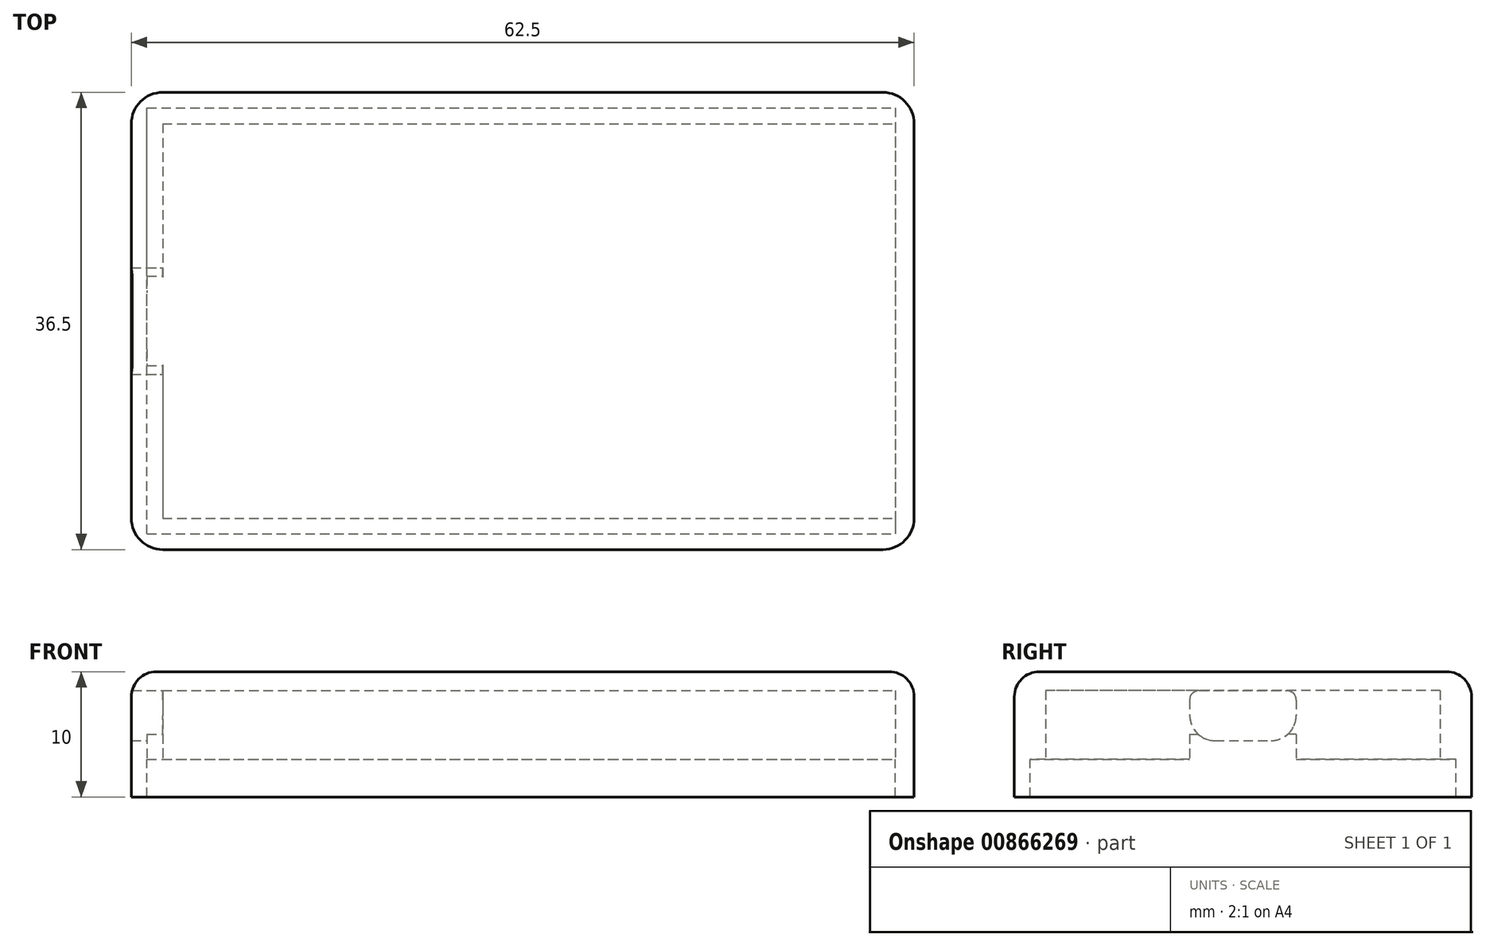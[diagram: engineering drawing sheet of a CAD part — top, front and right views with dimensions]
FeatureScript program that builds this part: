
annotation { "Feature Type Name" : "Feature", "Feature Type Description" : "" }
export const myFeature = defineFeature(function(context is Context, id is Id, definition is map)
    precondition{}
    {
        {
            var Q0;
            Q0=qCreatedBy(makeId("Top.planeOp"),FACE);
            var sketch = newSketch(context, id + "F0", { "sketchPlane" : qUnion([Q0])});
            skLineSegment(sketch, "E0.bottom", {"start": v(-30.75, 18.75) * mm, "end": v(31.75, 18.75) * mm});
            skLineSegment(sketch, "E0.top", {"start": v(-30.75, -17.75) * mm, "end": v(31.75, -17.75) * mm});
            skLineSegment(sketch, "E0.left", {"start": v(-30.75, 18.75) * mm, "end": v(-30.75, -17.75) * mm});
            skLineSegment(sketch, "E0.right", {"start": v(31.75, 18.75) * mm, "end": v(31.75, -17.75) * mm});
            skLineSegment(sketch, "E1.bottom", {"start": v(-28.25, 16.25) * mm, "end": v(30.25, 16.25) * mm});
            skLineSegment(sketch, "E1.top", {"start": v(-28.25, -15.25) * mm, "end": v(30.25, -15.25) * mm});
            skLineSegment(sketch, "E1.left", {"start": v(-28.25, 16.25) * mm, "end": v(-28.25, -15.25) * mm});
            skLineSegment(sketch, "E1.right", {"start": v(30.25, 16.25) * mm, "end": v(30.25, -15.25) * mm});
            skSolve(sketch);
        }
        {
            var Q0;
            Q0=makeQuery(id+"F0.imprint","IMPRINT",FACE,{"disambiguationData":[TD([[makeQuery(id+"F0.imprint","IMPRINT",EDGE,{"derivedFrom":sQuery(id+"F0.wireOp",EDGE,"E0.bottom")}),-1.0]])]});
            extrude(context, id + "F1", {"entities" : qUnion([Q0]), "depth" : 7 * mm});
        }
        {
            var Q0;
            Q0=makeQuery(id+"F1.opExtrude","CAP_FACE",FACE,{"disambiguationData":[OSD([sQuery(id+"F0.wireOp",EDGE,"E0.bottom"),sQuery(id+"F0.wireOp",EDGE,"E0.top"),sQuery(id+"F0.wireOp",EDGE,"E0.left"),sQuery(id+"F0.wireOp",EDGE,"E0.right"),sQuery(id+"F0.wireOp",EDGE,"E1.bottom"),sQuery(id+"F0.wireOp",EDGE,"E1.top"),sQuery(id+"F0.wireOp",EDGE,"E1.left"),sQuery(id+"F0.wireOp",EDGE,"E1.right")])],"isStart":false});
            var sketch = newSketch(context, id + "F2", { "sketchPlane" : qUnion([Q0])});
            skLineSegment(sketch, "E2.bottom", {"start": v(-28.25, 16.25) * mm, "end": v(30.25, 16.25) * mm});
            skLineSegment(sketch, "E2.top", {"start": v(-28.25, -15.25) * mm, "end": v(30.25, -15.25) * mm});
            skLineSegment(sketch, "E2.left", {"start": v(-28.25, 16.25) * mm, "end": v(-28.25, -15.25) * mm});
            skLineSegment(sketch, "E3", {"start": v(30.25, 16.25) * mm, "end": v(30.25, 7) * mm});
            skLineSegment(sketch, "E4", {"start": v(30.25, -6) * mm, "end": v(30.25, -15.25) * mm});
            skSolve(sketch);
        }
        {
            var Q0;
            Q0=makeQuery(id+"F2.imprint","IMPRINT",FACE,{"disambiguationData":[TD([[makeQuery(id+"F2.imprint","IMPRINT",EDGE,{"derivedFrom":sQuery(id+"F2.wireOp",EDGE,"E2.bottom")}),-1.0]])]});
            extrude(context, id + "F3", {"entities" : qUnion([Q0]), "operationType" : NewBodyOperationType.ADD, "oppositeDirection" : true, "depth" : 1.5 * mm});
        }
        {
            var Q0;
            Q0=makeQuery(id+"F1.opExtrude","CAP_FACE",FACE,{"disambiguationData":[OSD([sQuery(id+"F0.wireOp",EDGE,"E0.bottom"),sQuery(id+"F0.wireOp",EDGE,"E0.top"),sQuery(id+"F0.wireOp",EDGE,"E0.left"),sQuery(id+"F0.wireOp",EDGE,"E0.right"),sQuery(id+"F0.wireOp",EDGE,"E1.bottom"),sQuery(id+"F0.wireOp",EDGE,"E1.top"),sQuery(id+"F0.wireOp",EDGE,"E1.left"),sQuery(id+"F0.wireOp",EDGE,"E1.right")])],"isStart":true});
            var sketch = newSketch(context, id + "F4", { "sketchPlane" : qUnion([Q0])});
            skLineSegment(sketch, "E5.bottom", {"start": v(-30.75, 17.75) * mm, "end": v(31.75, 17.75) * mm});
            skLineSegment(sketch, "E5.top", {"start": v(-30.75, -18.75) * mm, "end": v(31.75, -18.75) * mm});
            skLineSegment(sketch, "E5.left", {"start": v(-30.75, 17.75) * mm, "end": v(-30.75, -18.75) * mm});
            skLineSegment(sketch, "E5.right", {"start": v(31.75, 17.75) * mm, "end": v(31.75, -18.75) * mm});
            skLineSegment(sketch, "E6.bottom", {"start": v(-29.5, 16.5) * mm, "end": v(30.25, 16.5) * mm});
            skLineSegment(sketch, "E6.top", {"start": v(-29.5, -17.52) * mm, "end": v(30.25, -17.52) * mm});
            skLineSegment(sketch, "E6.left", {"start": v(-29.5, 16.5) * mm, "end": v(-29.5, -17.52) * mm});
            skLineSegment(sketch, "E6.right", {"start": v(30.25, 16.5) * mm, "end": v(30.25, -17.52) * mm});
            skSolve(sketch);
        }
        {
            var Q0;
            Q0=makeQuery(id+"F4.imprint","IMPRINT",FACE,{"disambiguationData":[TD([[makeQuery(id+"F4.imprint","IMPRINT",EDGE,{"derivedFrom":sQuery(id+"F4.wireOp",EDGE,"E5.bottom")}),-1.0]])]});
            var Q1;
            {var subQ5=makeQuery(id+"F1.opExtrude","CAP_EDGE",EDGE,{"disambiguationData":[OSD([sQuery(id+"F0.wireOp",EDGE,"E1.right")])],"isStart":true});Q1=makeQuery(id+"F4.imprint","IMPRINT",FACE,{"disambiguationData":[TD([[makeQuery(id+"F4.imprint","IMPRINT",EDGE,{"derivedFrom":subQ5}),1.0]])]});}
            extrude(context, id + "F5", {"entities" : qUnion([Q0, Q1]), "operationType" : NewBodyOperationType.ADD, "depth" : 3 * mm});
        }
        {
            var Q0;
            Q0=makeQuery(id+"F1.opExtrude","SWEPT_FACE",FACE,{"disambiguationData":[OSD([sQuery(id+"F0.wireOp",EDGE,"E1.left")])]});
            var sketch = newSketch(context, id + "F6", { "sketchPlane" : qUnion([Q0])});
            skLineSegment(sketch, "E7.bottom", {"start": v(-3, 5.5) * mm, "end": v(4, 5.5) * mm});
            skLineSegment(sketch, "E7.top", {"start": v(-1.75, 1.5) * mm, "end": v(2.75, 1.5) * mm});
            skLineSegment(sketch, "E7.left", {"start": v(-3.75, 4.75) * mm, "end": v(-3.75, 3.5) * mm});
            skLineSegment(sketch, "E7.right", {"start": v(4.75, 4.75) * mm, "end": v(4.75, 3.5) * mm});
            skPoint(sketch, "E8.visualSharp", {"position": v(-3.75, 1.5) * mm});
            skArc(sketch, "E8.filletArc", {"start": v(-3.75, 3.5) * mm, "mid": v(-3.16, 2.09) * mm, "end": v(-1.75, 1.5) * mm});
            skPoint(sketch, "E9.visualSharp", {"position": v(4.75, 1.5) * mm});
            skArc(sketch, "E9.filletArc", {"start": v(2.75, 1.5) * mm, "mid": v(4.16, 2.09) * mm, "end": v(4.75, 3.5) * mm});
            skPoint(sketch, "E10.visualSharp", {"position": v(4.75, 5.5) * mm});
            skArc(sketch, "E10.filletArc", {"start": v(4.75, 4.75) * mm, "mid": v(4.53, 5.28) * mm, "end": v(4, 5.5) * mm});
            skPoint(sketch, "E11.visualSharp", {"position": v(-3.75, 5.5) * mm});
            skArc(sketch, "E11.filletArc", {"start": v(-3, 5.5) * mm, "mid": v(-3.53, 5.28) * mm, "end": v(-3.75, 4.75) * mm});
            skSolve(sketch);
        }
        {
            var Q0;
            Q0=makeQuery(id+"F6.imprint","IMPRINT",FACE,{"disambiguationData":[TD([[makeQuery(id+"F6.imprint","IMPRINT",EDGE,{"derivedFrom":sQuery(id+"F6.wireOp",EDGE,"E7.bottom")}),1.0]])]});
            extrude(context, id + "F7", {"entities" : qUnion([Q0]), "operationType" : NewBodyOperationType.REMOVE, "oppositeDirection" : true, "depth" : 2.5 * mm});
        }
        {
            var Q0;
            Q0=makeQuery(id+"F5.boolean.opBoolean","MERGE",EDGE,{"derivedFrom":[makeQuery(id+"F1.opExtrude","SWEPT_EDGE",EDGE,{"disambiguationData":[OSD([sQuery(id+"F0.wireOp",EDGE,"E0.bottom"),sQuery(id+"F0.wireOp",EDGE,"E0.left")])]}),makeQuery(id+"F5.opExtrude","SWEPT_EDGE",EDGE,{"disambiguationData":[OSD([sQuery(id+"F4.wireOp",EDGE,"E5.top"),sQuery(id+"F4.wireOp",EDGE,"E5.left")])]})]});
            var Q1;
            Q1=makeQuery(id+"F5.boolean.opBoolean","MERGE",EDGE,{"derivedFrom":[makeQuery(id+"F1.opExtrude","SWEPT_EDGE",EDGE,{"disambiguationData":[OSD([sQuery(id+"F0.wireOp",EDGE,"E0.top"),sQuery(id+"F0.wireOp",EDGE,"E0.left")])]}),makeQuery(id+"F5.opExtrude","SWEPT_EDGE",EDGE,{"disambiguationData":[OSD([sQuery(id+"F4.wireOp",EDGE,"E5.bottom"),sQuery(id+"F4.wireOp",EDGE,"E5.left")])]})]});
            var Q2;
            Q2=makeQuery(id+"F5.boolean.opBoolean","MERGE",EDGE,{"derivedFrom":[makeQuery(id+"F1.opExtrude","SWEPT_EDGE",EDGE,{"disambiguationData":[OSD([sQuery(id+"F0.wireOp",EDGE,"E0.bottom"),sQuery(id+"F0.wireOp",EDGE,"E0.right")])]}),makeQuery(id+"F5.opExtrude","SWEPT_EDGE",EDGE,{"disambiguationData":[OSD([sQuery(id+"F4.wireOp",EDGE,"E5.top"),sQuery(id+"F4.wireOp",EDGE,"E5.right")])]})]});
            var Q3;
            Q3=makeQuery(id+"F5.boolean.opBoolean","MERGE",EDGE,{"derivedFrom":[makeQuery(id+"F1.opExtrude","SWEPT_EDGE",EDGE,{"disambiguationData":[OSD([sQuery(id+"F0.wireOp",EDGE,"E0.top"),sQuery(id+"F0.wireOp",EDGE,"E0.right")])]}),makeQuery(id+"F5.opExtrude","SWEPT_EDGE",EDGE,{"disambiguationData":[OSD([sQuery(id+"F4.wireOp",EDGE,"E5.bottom"),sQuery(id+"F4.wireOp",EDGE,"E5.right")])]})]});
            fillet(context, id + "F8", {"entities" : qUnion([Q0, Q1, Q2, Q3]), "radius" : 2.5 * mm, "tangentPropagation" : true, "allowEdgeOverflow" : false});
        }
        {
            var Q0;
            Q0=makeQuery(id+"F1.opExtrude","CAP_EDGE",EDGE,{"disambiguationData":[OSD([sQuery(id+"F0.wireOp",EDGE,"E0.top")])],"isStart":false});
            fillet(context, id + "F9", {"entities" : qUnion([Q0]), "radius" : 2 * mm, "tangentPropagation" : true, "allowEdgeOverflow" : false});
        }
        {
            var Q0;
            Q0=makeQuery(id+"F1.opExtrude","CAP_FACE",FACE,{"disambiguationData":[OSD([sQuery(id+"F0.wireOp",EDGE,"E0.bottom"),sQuery(id+"F0.wireOp",EDGE,"E0.top"),sQuery(id+"F0.wireOp",EDGE,"E0.left"),sQuery(id+"F0.wireOp",EDGE,"E0.right"),sQuery(id+"F0.wireOp",EDGE,"E1.bottom"),sQuery(id+"F0.wireOp",EDGE,"E1.top"),sQuery(id+"F0.wireOp",EDGE,"E1.left"),sQuery(id+"F0.wireOp",EDGE,"E1.right")])],"isStart":true});
            var sketch = newSketch(context, id + "F10", { "sketchPlane" : qUnion([Q0])});
            skLineSegment(sketch, "E12.bottom", {"start": v(-29.5, 3.75) * mm, "end": v(-28.25, 3.75) * mm});
            skLineSegment(sketch, "E12.top", {"start": v(-29.5, -4.75) * mm, "end": v(-28.25, -4.75) * mm});
            skLineSegment(sketch, "E12.left", {"start": v(-29.5, 3.75) * mm, "end": v(-29.5, -4.75) * mm});
            skLineSegment(sketch, "E12.right", {"start": v(-28.25, 3.75) * mm, "end": v(-28.25, -4.75) * mm});
            skSolve(sketch);
        }
        {
            var Q0;
            Q0=makeQuery(id+"F10.imprint","IMPRINT",FACE,{"disambiguationData":[TD([[makeQuery(id+"F10.imprint","IMPRINT",EDGE,{"derivedFrom":sQuery(id+"F10.wireOp",EDGE,"E12.bottom")}),-1.0]])]});
            extrude(context, id + "F11", {"entities" : qUnion([Q0]), "operationType" : NewBodyOperationType.REMOVE, "oppositeDirection" : true, "depth" : 2 * mm});
        }
    });
